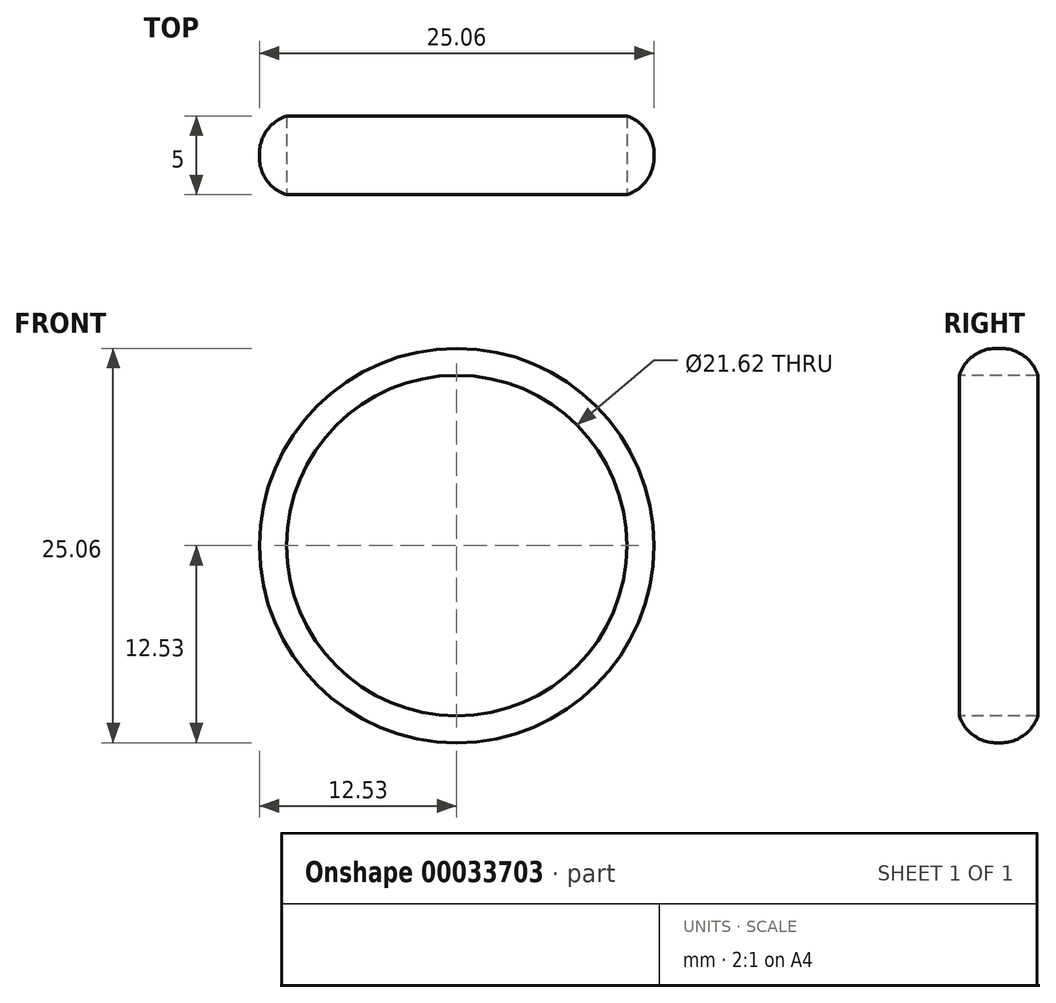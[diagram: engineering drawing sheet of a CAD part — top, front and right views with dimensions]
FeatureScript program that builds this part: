
annotation { "Feature Type Name" : "Feature", "Feature Type Description" : "" }
export const myFeature = defineFeature(function(context is Context, id is Id, definition is map)
    precondition{}
    {
        {
            var Q0;
            Q0=qCreatedBy(makeId("Front.planeOp"),FACE);
            var sketch = newSketch(context, id + "F0", { "sketchPlane" : qUnion([Q0])});
            skCircle(sketch, "E0", {"center": v(0, 0) * mm, "radius": 12.53 * mm});
            skSolve(sketch);
        }
        {
            var Q0;
            Q0=makeQuery(id+"F0.imprint","IMPRINT",FACE,{"disambiguationData":[TD([[makeQuery(id+"F0.imprint","IMPRINT",EDGE,{"derivedFrom":sQuery(id+"F0.wireOp",EDGE,"E0")}),1.0]])]});
            extrude(context, id + "F1", {"entities" : qUnion([Q0]), "endBound" : BoundingType.SYMMETRIC, "depth" : 5 * mm});
        }
        {
            var Q0;
            Q0=makeQuery(id+"F1.opExtrude","CAP_FACE",FACE,{"disambiguationData":[OSD([sQuery(id+"F0.wireOp",EDGE,"E0")])],"isStart":false});
            var sketch = newSketch(context, id + "F2", { "sketchPlane" : qUnion([Q0])});
            skCircle(sketch, "E1", {"center": v(0, 0) * mm, "radius": 10.8 * mm});
            skSolve(sketch);
        }
        {
            var Q0;
            Q0=makeQuery(id+"F2.imprint","IMPRINT",FACE,{"disambiguationData":[TD([[makeQuery(id+"F2.imprint","IMPRINT",EDGE,{"derivedFrom":sQuery(id+"F2.wireOp",EDGE,"E1")}),1.0]])]});
            extrude(context, id + "F3", {"entities" : qUnion([Q0]), "operationType" : NewBodyOperationType.REMOVE, "oppositeDirection" : true, "depth" : 75.99 * mm});
        }
        {
            var Q0;
            Q0=makeQuery(id+"F1.opExtrude","CAP_EDGE",EDGE,{"disambiguationData":[OSD([sQuery(id+"F0.wireOp",EDGE,"E0")])],"isStart":false});
            fillet(context, id + "F4", {"entities" : qUnion([Q0]), "radius" : 2.5 * mm, "tangentPropagation" : true, "allowEdgeOverflow" : false});
        }
        {
            var Q0;
            Q0=makeQuery(id+"F1.opExtrude","CAP_EDGE",EDGE,{"disambiguationData":[OSD([sQuery(id+"F0.wireOp",EDGE,"E0")])],"isStart":true});
            fillet(context, id + "F5", {"entities" : qUnion([Q0]), "radius" : 2.5 * mm, "tangentPropagation" : true, "allowEdgeOverflow" : false});
        }
    });
